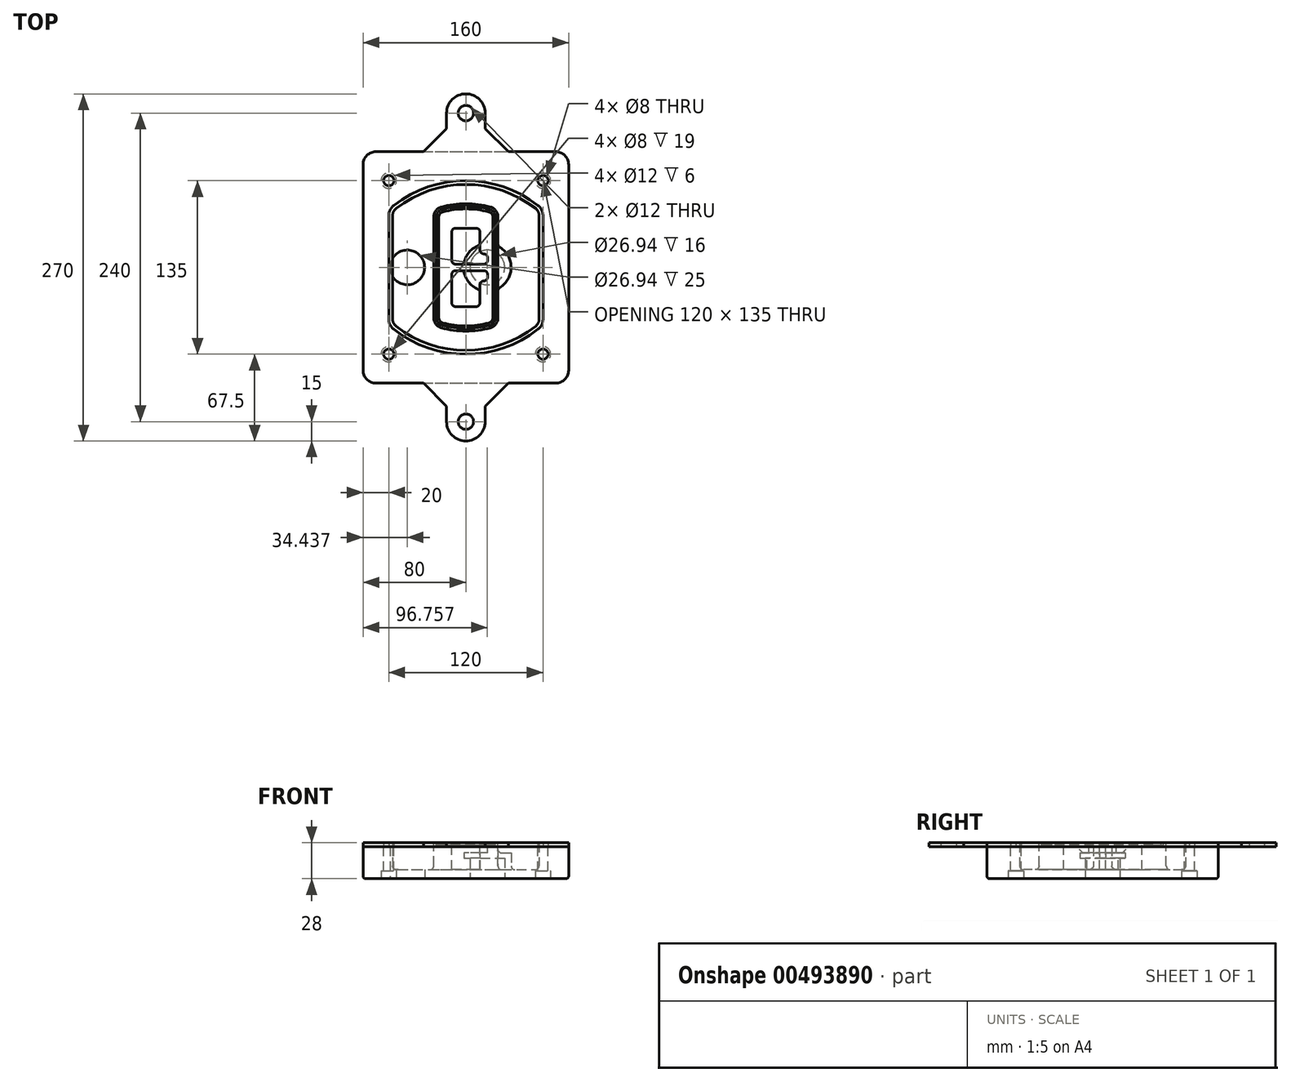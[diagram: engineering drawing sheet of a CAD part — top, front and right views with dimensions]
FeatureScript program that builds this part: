
annotation { "Feature Type Name" : "Feature", "Feature Type Description" : "" }
export const myFeature = defineFeature(function(context is Context, id is Id, definition is map)
    precondition{}
    {
        {
            var Q0;
            Q0=qCreatedBy(makeId("Top.planeOp"),FACE);
            var sketch = newSketch(context, id + "F0", { "sketchPlane" : qUnion([Q0])});
            skPoint(sketch, "E0.rect.middle", {"position": v(0, 0) * mm});
            skLineSegment(sketch, "E1.bottom", {"start": v(-70, -90) * mm, "end": v(70, -90) * mm});
            skLineSegment(sketch, "E1.top", {"start": v(-70, 90) * mm, "end": v(70, 90) * mm});
            skLineSegment(sketch, "E1.left", {"start": v(-80, -80) * mm, "end": v(-80, 80) * mm});
            skLineSegment(sketch, "E1.right", {"start": v(80, -80) * mm, "end": v(80, 80) * mm});
            skLineSegment(sketch, "E2", {"start": v(-80, 90) * mm, "end": v(80, -90) * mm, "construction": true});
            skLineSegment(sketch, "E3", {"start": v(80, 90) * mm, "end": v(-80, -90) * mm, "construction": true});
            skCircle(sketch, "E4", {"center": v(-60, 67.5) * mm, "radius": 4 * mm});
            skCircle(sketch, "E5", {"center": v(60, 67.5) * mm, "radius": 4 * mm});
            skCircle(sketch, "E6", {"center": v(60, -67.5) * mm, "radius": 4 * mm});
            skCircle(sketch, "E7", {"center": v(-60, -67.5) * mm, "radius": 4 * mm});
            skLineSegment(sketch, "E8", {"start": v(-60, 67.5) * mm, "end": v(60, 67.5) * mm, "construction": true});
            skLineSegment(sketch, "E9", {"start": v(60, 67.5) * mm, "end": v(60, -67.5) * mm, "construction": true});
            skLineSegment(sketch, "E10", {"start": v(60, -67.5) * mm, "end": v(-60, -67.5) * mm, "construction": true});
            skLineSegment(sketch, "E11", {"start": v(-60, -67.5) * mm, "end": v(-60, 67.5) * mm, "construction": true});
            skLineSegment(sketch, "E12", {"start": v(-60, 40.3) * mm, "end": v(-60, -40.3) * mm});
            skLineSegment(sketch, "E13", {"start": v(60, 40.3) * mm, "end": v(60, -40.3) * mm});
            skArc(sketch, "E14", {"start": v(56.15, 48.18) * mm, "mid": v(0, 67.5) * mm, "end": v(-56.15, 48.18) * mm});
            skArc(sketch, "E15", {"start": v(-56.15, -48.18) * mm, "mid": v(0, -67.5) * mm, "end": v(56.15, -48.18) * mm});
            skLineSegment(sketch, "E16", {"start": v(-60, 0) * mm, "end": v(60, 0) * mm, "construction": true});
            skPoint(sketch, "E17.visualSharp", {"position": v(-60, -45) * mm});
            skArc(sketch, "E17.filletArc", {"start": v(-60, -40.3) * mm, "mid": v(-58.99, -44.68) * mm, "end": v(-56.15, -48.18) * mm});
            skPoint(sketch, "E18.visualSharp", {"position": v(-60, 45) * mm});
            skArc(sketch, "E18.filletArc", {"start": v(-56.15, 48.18) * mm, "mid": v(-58.99, 44.68) * mm, "end": v(-60, 40.3) * mm});
            skPoint(sketch, "E19.visualSharp", {"position": v(60, 45) * mm});
            skArc(sketch, "E19.filletArc", {"start": v(60, 40.3) * mm, "mid": v(58.99, 44.68) * mm, "end": v(56.15, 48.18) * mm});
            skPoint(sketch, "E20.visualSharp", {"position": v(60, -45) * mm});
            skArc(sketch, "E20.filletArc", {"start": v(56.15, -48.18) * mm, "mid": v(58.99, -44.68) * mm, "end": v(60, -40.3) * mm});
            skPoint(sketch, "E21.visualSharp", {"position": v(-80, 90) * mm});
            skArc(sketch, "E21.filletArc", {"start": v(-70, 90) * mm, "mid": v(-77.07, 87.07) * mm, "end": v(-80, 80) * mm});
            skPoint(sketch, "E22.visualSharp", {"position": v(80, 90) * mm});
            skArc(sketch, "E22.filletArc", {"start": v(80, 80) * mm, "mid": v(77.07, 87.07) * mm, "end": v(70, 90) * mm});
            skPoint(sketch, "E23.visualSharp", {"position": v(80, -90) * mm});
            skArc(sketch, "E23.filletArc", {"start": v(70, -90) * mm, "mid": v(77.07, -87.07) * mm, "end": v(80, -80) * mm});
            skPoint(sketch, "E24.visualSharp", {"position": v(-80, -90) * mm});
            skArc(sketch, "E24.filletArc", {"start": v(-80, -80) * mm, "mid": v(-77.07, -87.07) * mm, "end": v(-70, -90) * mm});
            skArc(sketch, "E25.0", {"start": v(57, 40.3) * mm, "mid": v(56.3, 43.36) * mm, "end": v(54.3, 45.81) * mm});
            skLineSegment(sketch, "E25.1", {"start": v(57, 40.3) * mm, "end": v(57, -40.3) * mm});
            skArc(sketch, "E25.2", {"start": v(54.3, -45.81) * mm, "mid": v(56.3, -43.36) * mm, "end": v(57, -40.3) * mm});
            skArc(sketch, "E25.3", {"start": v(-54.3, -45.81) * mm, "mid": v(0, -64.5) * mm, "end": v(54.3, -45.81) * mm});
            skArc(sketch, "E25.4", {"start": v(-57, -40.3) * mm, "mid": v(-56.3, -43.36) * mm, "end": v(-54.3, -45.81) * mm});
            skArc(sketch, "E25.5", {"start": v(54.3, 45.81) * mm, "mid": v(0, 64.5) * mm, "end": v(-54.3, 45.81) * mm});
            skLineSegment(sketch, "E25.6", {"start": v(-57, 40.3) * mm, "end": v(-57, -40.3) * mm});
            skArc(sketch, "E25.7", {"start": v(-54.3, 45.81) * mm, "mid": v(-56.3, 43.36) * mm, "end": v(-57, 40.3) * mm});
            skArc(sketch, "E26.0", {"start": v(-58.62, 51.33) * mm, "mid": v(-62.58, 46.43) * mm, "end": v(-64, 40.3) * mm});
            skArc(sketch, "E26.1", {"start": v(58.62, 51.33) * mm, "mid": v(0, 71.5) * mm, "end": v(-58.62, 51.33) * mm});
            skArc(sketch, "E26.2", {"start": v(64, 40.3) * mm, "mid": v(62.58, 46.43) * mm, "end": v(58.62, 51.33) * mm});
            skLineSegment(sketch, "E26.3", {"start": v(64, 40.3) * mm, "end": v(64, -40.3) * mm});
            skArc(sketch, "E26.4", {"start": v(58.62, -51.33) * mm, "mid": v(62.58, -46.43) * mm, "end": v(64, -40.3) * mm});
            skLineSegment(sketch, "E26.5", {"start": v(-64, 40.3) * mm, "end": v(-64, -40.3) * mm});
            skArc(sketch, "E26.6", {"start": v(-58.62, -51.33) * mm, "mid": v(0, -71.5) * mm, "end": v(58.62, -51.33) * mm});
            skArc(sketch, "E26.7", {"start": v(-64, -40.3) * mm, "mid": v(-62.58, -46.43) * mm, "end": v(-58.62, -51.33) * mm});
            skSolve(sketch);
        }
        {
            var Q0;
            Q0=makeQuery(id+"F0.imprint","IMPRINT",FACE,{"disambiguationData":[TD([[makeQuery(id+"F0.imprint","IMPRINT",EDGE,{"derivedFrom":sQuery(id+"F0.wireOp",EDGE,"E1.bottom")}),1.0]])]});
            var Q1;
            Q1=makeQuery(id+"F0.imprint","IMPRINT",FACE,{"disambiguationData":[TD([[makeQuery(id+"F0.imprint","IMPRINT",EDGE,{"derivedFrom":sQuery(id+"F0.wireOp",EDGE,"E12")}),1.0]])]});
            var Q2;
            Q2=makeQuery(id+"F0.imprint","IMPRINT",FACE,{"disambiguationData":[TD([[makeQuery(id+"F0.imprint","IMPRINT",EDGE,{"derivedFrom":sQuery(id+"F0.wireOp",EDGE,"E25.0")}),1.0]])]});
            var Q3;
            Q3=makeQuery(id+"F0.imprint","IMPRINT",FACE,{"disambiguationData":[TD([[makeQuery(id+"F0.imprint","IMPRINT",EDGE,{"derivedFrom":sQuery(id+"F0.wireOp",EDGE,"E12")}),-1.0]])]});
            extrude(context, id + "F1", {"entities" : qUnion([Q0, Q1, Q2, Q3]), "oppositeDirection" : true, "depth" : 25 * mm});
        }
        {
            var Q0;
            Q0=makeQuery(id+"F0.imprint","IMPRINT",FACE,{"disambiguationData":[TD([[makeQuery(id+"F0.imprint","IMPRINT",EDGE,{"derivedFrom":sQuery(id+"F0.wireOp",EDGE,"E12")}),1.0]])]});
            extrude(context, id + "F2", {"entities" : qUnion([Q0]), "operationType" : NewBodyOperationType.ADD, "depth" : 3 * mm});
        }
        {
            var Q0;
            Q0=makeQuery(id+"F0.imprint","IMPRINT",FACE,{"disambiguationData":[TD([[makeQuery(id+"F0.imprint","IMPRINT",EDGE,{"derivedFrom":sQuery(id+"F0.wireOp",EDGE,"E25.0")}),1.0]])]});
            extrude(context, id + "F3", {"entities" : qUnion([Q0]), "operationType" : NewBodyOperationType.REMOVE, "oppositeDirection" : true, "depth" : 18 * mm});
        }
        {
            var Q0;
            Q0=makeQuery(id+"F2.opExtrude","CAP_FACE",FACE,{"disambiguationData":[OSD([sQuery(id+"F0.wireOp",EDGE,"E12"),sQuery(id+"F0.wireOp",EDGE,"E13"),sQuery(id+"F0.wireOp",EDGE,"E14"),sQuery(id+"F0.wireOp",EDGE,"E15"),sQuery(id+"F0.wireOp",EDGE,"E17.filletArc"),sQuery(id+"F0.wireOp",EDGE,"E18.filletArc"),sQuery(id+"F0.wireOp",EDGE,"E19.filletArc"),sQuery(id+"F0.wireOp",EDGE,"E20.filletArc"),sQuery(id+"F0.wireOp",EDGE,"E25.0"),sQuery(id+"F0.wireOp",EDGE,"E25.1"),sQuery(id+"F0.wireOp",EDGE,"E25.2"),sQuery(id+"F0.wireOp",EDGE,"E25.3"),sQuery(id+"F0.wireOp",EDGE,"E25.4"),sQuery(id+"F0.wireOp",EDGE,"E25.5"),sQuery(id+"F0.wireOp",EDGE,"E25.6"),sQuery(id+"F0.wireOp",EDGE,"E25.7")])],"isStart":false});
            var sketch = newSketch(context, id + "F4", { "sketchPlane" : qUnion([Q0])});
            skArc(sketch, "E27.0", {"start": v(-19.08, -46.97) * mm, "mid": v(0, -49.5) * mm, "end": v(19.08, -46.97) * mm});
            skArc(sketch, "E28.0", {"start": v(19.08, 46.97) * mm, "mid": v(0, 49.5) * mm, "end": v(-19.08, 46.97) * mm});
            skLineSegment(sketch, "E29", {"start": v(-25, 39.25) * mm, "end": v(-25, -39.25) * mm});
            skLineSegment(sketch, "E30", {"start": v(25, 39.25) * mm, "end": v(25, -39.25) * mm});
            skLineSegment(sketch, "E31", {"start": v(-25, 45.1) * mm, "end": v(25, 45.1) * mm, "construction": true});
            skLineSegment(sketch, "E32", {"start": v(-25, -45.1) * mm, "end": v(25, -45.1) * mm, "construction": true});
            skPoint(sketch, "E33.visualSharp", {"position": v(-25, 45.1) * mm});
            skArc(sketch, "E33.filletArc", {"start": v(-19.08, 46.97) * mm, "mid": v(-23.35, 44.11) * mm, "end": v(-25, 39.25) * mm});
            skPoint(sketch, "E34.visualSharp", {"position": v(25, 45.1) * mm});
            skArc(sketch, "E34.filletArc", {"start": v(25, 39.25) * mm, "mid": v(23.35, 44.11) * mm, "end": v(19.08, 46.97) * mm});
            skPoint(sketch, "E35.visualSharp", {"position": v(25, -45.1) * mm});
            skArc(sketch, "E35.filletArc", {"start": v(19.08, -46.97) * mm, "mid": v(23.35, -44.11) * mm, "end": v(25, -39.25) * mm});
            skPoint(sketch, "E36.visualSharp", {"position": v(-25, -45.1) * mm});
            skArc(sketch, "E36.filletArc", {"start": v(-25, -39.25) * mm, "mid": v(-23.35, -44.11) * mm, "end": v(-19.08, -46.97) * mm});
            skArc(sketch, "E37.0", {"start": v(54.3, 45.81) * mm, "mid": v(0, 64.5) * mm, "end": v(-54.3, 45.81) * mm});
            skArc(sketch, "E37.1", {"start": v(-54.3, 45.81) * mm, "mid": v(-56.3, 43.36) * mm, "end": v(-57, 40.3) * mm});
            skLineSegment(sketch, "E37.2", {"start": v(-57, 40.3) * mm, "end": v(-57, -40.3) * mm});
            skArc(sketch, "E37.3", {"start": v(-57, -40.3) * mm, "mid": v(-56.3, -43.36) * mm, "end": v(-54.3, -45.81) * mm});
            skArc(sketch, "E37.4", {"start": v(-54.3, -45.81) * mm, "mid": v(0, -64.5) * mm, "end": v(54.3, -45.81) * mm});
            skArc(sketch, "E37.5", {"start": v(54.3, -45.81) * mm, "mid": v(56.3, -43.36) * mm, "end": v(57, -40.3) * mm});
            skLineSegment(sketch, "E37.6", {"start": v(57, 40.3) * mm, "end": v(57, -40.3) * mm});
            skArc(sketch, "E37.7", {"start": v(57, 40.3) * mm, "mid": v(56.3, 43.36) * mm, "end": v(54.3, 45.81) * mm});
            skLineSegment(sketch, "E38.0", {"start": v(23, 39.25) * mm, "end": v(23, -39.25) * mm});
            skArc(sketch, "E38.1", {"start": v(18.56, -45.04) * mm, "mid": v(21.76, -42.9) * mm, "end": v(23, -39.25) * mm});
            skArc(sketch, "E38.2", {"start": v(-18.56, -45.04) * mm, "mid": v(0, -47.5) * mm, "end": v(18.56, -45.04) * mm});
            skArc(sketch, "E38.3", {"start": v(-23, -39.25) * mm, "mid": v(-21.76, -42.9) * mm, "end": v(-18.56, -45.04) * mm});
            skLineSegment(sketch, "E38.4", {"start": v(-23, 39.25) * mm, "end": v(-23, -39.25) * mm});
            skArc(sketch, "E38.5", {"start": v(23, 39.25) * mm, "mid": v(21.76, 42.9) * mm, "end": v(18.56, 45.04) * mm});
            skArc(sketch, "E38.6", {"start": v(-18.56, 45.04) * mm, "mid": v(-21.76, 42.9) * mm, "end": v(-23, 39.25) * mm});
            skArc(sketch, "E38.7", {"start": v(18.56, 45.04) * mm, "mid": v(0, 47.5) * mm, "end": v(-18.56, 45.04) * mm});
            skArc(sketch, "E39.0", {"start": v(21, 39.25) * mm, "mid": v(20.18, 41.68) * mm, "end": v(18.04, 43.1) * mm});
            skLineSegment(sketch, "E39.1", {"start": v(21, 39.25) * mm, "end": v(21, -39.25) * mm});
            skArc(sketch, "E39.2", {"start": v(18.04, -43.1) * mm, "mid": v(20.18, -41.68) * mm, "end": v(21, -39.25) * mm});
            skArc(sketch, "E39.3", {"start": v(-18.04, -43.1) * mm, "mid": v(0, -45.5) * mm, "end": v(18.04, -43.1) * mm});
            skArc(sketch, "E39.4", {"start": v(-21, -39.25) * mm, "mid": v(-20.18, -41.68) * mm, "end": v(-18.04, -43.1) * mm});
            skArc(sketch, "E39.5", {"start": v(18.04, 43.1) * mm, "mid": v(0, 45.5) * mm, "end": v(-18.04, 43.1) * mm});
            skLineSegment(sketch, "E39.6", {"start": v(-21, 39.25) * mm, "end": v(-21, -39.25) * mm});
            skArc(sketch, "E39.7", {"start": v(-18.04, 43.1) * mm, "mid": v(-20.18, 41.68) * mm, "end": v(-21, 39.25) * mm});
            skLineSegment(sketch, "E40", {"start": v(-25, 0) * mm, "end": v(25, 0) * mm, "construction": true});
            skLineSegment(sketch, "E41", {"start": v(-11, 5.5) * mm, "end": v(-11, 27.5) * mm});
            skLineSegment(sketch, "E42", {"start": v(-8, 30.5) * mm, "end": v(8, 30.5) * mm});
            skLineSegment(sketch, "E43", {"start": v(11, 27.5) * mm, "end": v(11, 13.5) * mm});
            skLineSegment(sketch, "E44", {"start": v(14, 10.5) * mm, "end": v(14, 10.5) * mm});
            skLineSegment(sketch, "E45", {"start": v(17, 7.5) * mm, "end": v(17, 5.5) * mm});
            skLineSegment(sketch, "E46", {"start": v(14, 2.5) * mm, "end": v(-8, 2.5) * mm});
            skPoint(sketch, "E47.visualSharp", {"position": v(-11, 30.5) * mm});
            skArc(sketch, "E47.filletArc", {"start": v(-8, 30.5) * mm, "mid": v(-10.12, 29.62) * mm, "end": v(-11, 27.5) * mm});
            skPoint(sketch, "E48.visualSharp", {"position": v(11, 30.5) * mm});
            skArc(sketch, "E48.filletArc", {"start": v(11, 27.5) * mm, "mid": v(10.12, 29.62) * mm, "end": v(8, 30.5) * mm});
            skPoint(sketch, "E49.visualSharp", {"position": v(11, 10.5) * mm});
            skArc(sketch, "E49.filletArc", {"start": v(11, 13.5) * mm, "mid": v(11.88, 11.38) * mm, "end": v(14, 10.5) * mm});
            skPoint(sketch, "E50.visualSharp", {"position": v(17, 10.5) * mm});
            skArc(sketch, "E50.filletArc", {"start": v(17, 7.5) * mm, "mid": v(16.12, 9.62) * mm, "end": v(14, 10.5) * mm});
            skPoint(sketch, "E51.visualSharp", {"position": v(17, 2.5) * mm});
            skArc(sketch, "E51.filletArc", {"start": v(14, 2.5) * mm, "mid": v(16.12, 3.38) * mm, "end": v(17, 5.5) * mm});
            skPoint(sketch, "E52.visualSharp", {"position": v(-11, 2.5) * mm});
            skArc(sketch, "E52.filletArc", {"start": v(-11, 5.5) * mm, "mid": v(-10.12, 3.38) * mm, "end": v(-8, 2.5) * mm});
            skLineSegment(sketch, "E53.0.MirrorCS", {"start": v(14, -2.5) * mm, "end": v(-8, -2.5) * mm});
            skArc(sketch, "E54.0.MirrorCS", {"start": v(-11, -5.5) * mm, "mid": v(-10.12, -3.38) * mm, "end": v(-8, -2.5) * mm});
            skLineSegment(sketch, "E55.0.MirrorCS", {"start": v(-11, -5.5) * mm, "end": v(-11, -27.5) * mm});
            skArc(sketch, "E56.0.MirrorCS", {"start": v(-8, -30.5) * mm, "mid": v(-10.12, -29.62) * mm, "end": v(-11, -27.5) * mm});
            skLineSegment(sketch, "E57.0.MirrorCS", {"start": v(-8, -30.5) * mm, "end": v(8, -30.5) * mm});
            skArc(sketch, "E58.0.MirrorCS", {"start": v(11, -27.5) * mm, "mid": v(10.12, -29.62) * mm, "end": v(8, -30.5) * mm});
            skLineSegment(sketch, "E59.0.MirrorCS", {"start": v(11, -27.5) * mm, "end": v(11, -13.5) * mm});
            skArc(sketch, "E60.0.MirrorCS", {"start": v(11, -13.5) * mm, "mid": v(11.88, -11.38) * mm, "end": v(14, -10.5) * mm});
            skArc(sketch, "E61.0.MirrorCS", {"start": v(17, -7.5) * mm, "mid": v(16.12, -9.62) * mm, "end": v(14, -10.5) * mm});
            skLineSegment(sketch, "E62.0.MirrorCS", {"start": v(17, -7.5) * mm, "end": v(17, -5.5) * mm});
            skArc(sketch, "E63.0.MirrorCS", {"start": v(14, -2.5) * mm, "mid": v(16.12, -3.38) * mm, "end": v(17, -5.5) * mm});
            skSolve(sketch);
        }
        {
            var Q0;
            Q0=makeQuery(id+"F4.imprint","IMPRINT",FACE,{"disambiguationData":[TD([[makeQuery(id+"F4.imprint","IMPRINT",EDGE,{"derivedFrom":sQuery(id+"F4.wireOp",EDGE,"E27.0")}),1.0]])]});
            var Q1;
            Q1=makeQuery(id+"F4.imprint","IMPRINT",FACE,{"disambiguationData":[TD([[makeQuery(id+"F4.imprint","IMPRINT",EDGE,{"derivedFrom":sQuery(id+"F4.wireOp",EDGE,"E38.0")}),-1.0]])]});
            var Q2;
            Q2=makeQuery(id+"F4.imprint","IMPRINT",FACE,{"disambiguationData":[TD([[makeQuery(id+"F4.imprint","IMPRINT",EDGE,{"derivedFrom":sQuery(id+"F4.wireOp",EDGE,"E39.0")}),1.0]])]});
            extrude(context, id + "F5", {"entities" : qUnion([Q0, Q1, Q2]), "operationType" : NewBodyOperationType.ADD, "endBound" : BoundingType.UP_TO_NEXT, "oppositeDirection" : true, "depth" : 25 * mm});
        }
        {
            var Q0;
            Q0=makeQuery(id+"F4.imprint","IMPRINT",FACE,{"disambiguationData":[TD([[makeQuery(id+"F4.imprint","IMPRINT",EDGE,{"derivedFrom":sQuery(id+"F4.wireOp",EDGE,"E38.0")}),-1.0]])]});
            extrude(context, id + "F6", {"entities" : qUnion([Q0]), "operationType" : NewBodyOperationType.REMOVE, "oppositeDirection" : true, "depth" : 2 * mm});
        }
        {
            var Q0;
            Q0=makeQuery(id+"F1.opExtrude","CAP_FACE",FACE,{"disambiguationData":[OSD([sQuery(id+"F0.wireOp",EDGE,"E1.bottom"),sQuery(id+"F0.wireOp",EDGE,"E1.top"),sQuery(id+"F0.wireOp",EDGE,"E1.left"),sQuery(id+"F0.wireOp",EDGE,"E1.right"),sQuery(id+"F0.wireOp",EDGE,"E4"),sQuery(id+"F0.wireOp",EDGE,"E5"),sQuery(id+"F0.wireOp",EDGE,"E6"),sQuery(id+"F0.wireOp",EDGE,"E7"),sQuery(id+"F0.wireOp",EDGE,"E21.filletArc"),sQuery(id+"F0.wireOp",EDGE,"E22.filletArc"),sQuery(id+"F0.wireOp",EDGE,"E23.filletArc"),sQuery(id+"F0.wireOp",EDGE,"E24.filletArc")])],"isStart":false});
            var sketch = newSketch(context, id + "F7", { "sketchPlane" : qUnion([Q0])});
            skCircle(sketch, "E64", {"center": v(16.76, 0) * mm, "radius": 13.47 * mm});
            skCircle(sketch, "E65", {"center": v(-45.56, 0) * mm, "radius": 13.47 * mm});
            skLineSegment(sketch, "E66", {"start": v(80, 0) * mm, "end": v(-80, 0) * mm});
            skCircle(sketch, "E67", {"center": v(16.76, 0) * mm, "radius": 18.47 * mm});
            skCircle(sketch, "E68", {"center": v(60, -67.5) * mm, "radius": 6 * mm});
            skCircle(sketch, "E69", {"center": v(-60, -67.5) * mm, "radius": 6 * mm});
            skCircle(sketch, "E70", {"center": v(-60, 67.5) * mm, "radius": 6 * mm});
            skCircle(sketch, "E71", {"center": v(60, 67.5) * mm, "radius": 6 * mm});
            skSolve(sketch);
        }
        {
            var Q0;
            {var subQ1=sQuery(id+"F7.wireOp",EDGE,"E66");var subQ4=sQuery(id+"F7.wireOp",EDGE,"E64");var subQ6=makeQuery(id+"F7.imprint","INTERSECT",VERTEX,{"disambiguationData":[OD(0.0)],"derivedFrom":[subQ4,subQ1]});Q0=makeQuery(id+"F7.imprint","IMPRINT",FACE,{"disambiguationData":[TD([[makeQuery(id+"F7.imprint","IMPRINT",EDGE,{"disambiguationData":[TD([[subQ6,-1.0]])],"derivedFrom":subQ4}),-1.0]])]});}
            var Q1;
            {var subQ0=sQuery(id+"F7.wireOp",EDGE,"E66");var subQ1=sQuery(id+"F7.wireOp",EDGE,"E64");var subQ3=makeQuery(id+"F7.imprint","INTERSECT",VERTEX,{"disambiguationData":[OD(0.0)],"derivedFrom":[subQ1,subQ0]});Q1=makeQuery(id+"F7.imprint","IMPRINT",FACE,{"disambiguationData":[TD([[makeQuery(id+"F7.imprint","IMPRINT",EDGE,{"disambiguationData":[TD([[subQ3,-1.0]])],"derivedFrom":subQ1}),1.0]])]});}
            var Q2;
            {var subQ0=sQuery(id+"F7.wireOp",EDGE,"E66");var subQ1=sQuery(id+"F7.wireOp",EDGE,"E64");var subQ3=makeQuery(id+"F7.imprint","INTERSECT",VERTEX,{"disambiguationData":[OD(0.0)],"derivedFrom":[subQ1,subQ0]});Q2=makeQuery(id+"F7.imprint","IMPRINT",FACE,{"disambiguationData":[TD([[makeQuery(id+"F7.imprint","IMPRINT",EDGE,{"disambiguationData":[TD([[subQ3,1.0]])],"derivedFrom":subQ1}),1.0]])]});}
            var Q3;
            {var subQ1=sQuery(id+"F7.wireOp",EDGE,"E66");var subQ4=sQuery(id+"F7.wireOp",EDGE,"E64");var subQ6=makeQuery(id+"F7.imprint","INTERSECT",VERTEX,{"disambiguationData":[OD(0.0)],"derivedFrom":[subQ4,subQ1]});Q3=makeQuery(id+"F7.imprint","IMPRINT",FACE,{"disambiguationData":[TD([[makeQuery(id+"F7.imprint","IMPRINT",EDGE,{"disambiguationData":[TD([[subQ6,1.0]])],"derivedFrom":subQ4}),-1.0]])]});}
            extrude(context, id + "F8", {"entities" : qUnion([Q0, Q1, Q2, Q3]), "operationType" : NewBodyOperationType.ADD, "oppositeDirection" : true, "depth" : 20 * mm});
        }
        {
            var Q0;
            {var subQ0=sQuery(id+"F7.wireOp",EDGE,"E66");var subQ1=sQuery(id+"F7.wireOp",EDGE,"E64");var subQ3=makeQuery(id+"F7.imprint","INTERSECT",VERTEX,{"disambiguationData":[OD(0.0)],"derivedFrom":[subQ1,subQ0]});Q0=makeQuery(id+"F7.imprint","IMPRINT",FACE,{"disambiguationData":[TD([[makeQuery(id+"F7.imprint","IMPRINT",EDGE,{"disambiguationData":[TD([[subQ3,-1.0]])],"derivedFrom":subQ1}),1.0]])]});}
            var Q1;
            {var subQ0=sQuery(id+"F7.wireOp",EDGE,"E66");var subQ1=sQuery(id+"F7.wireOp",EDGE,"E64");var subQ3=makeQuery(id+"F7.imprint","INTERSECT",VERTEX,{"disambiguationData":[OD(0.0)],"derivedFrom":[subQ1,subQ0]});Q1=makeQuery(id+"F7.imprint","IMPRINT",FACE,{"disambiguationData":[TD([[makeQuery(id+"F7.imprint","IMPRINT",EDGE,{"disambiguationData":[TD([[subQ3,1.0]])],"derivedFrom":subQ1}),1.0]])]});}
            extrude(context, id + "F9", {"entities" : qUnion([Q0, Q1]), "operationType" : NewBodyOperationType.REMOVE, "oppositeDirection" : true, "depth" : 16 * mm});
        }
        {
            var Q0;
            {var subQ0=sQuery(id+"F7.wireOp",EDGE,"E66");var subQ1=sQuery(id+"F7.wireOp",EDGE,"E65");var subQ3=makeQuery(id+"F7.imprint","INTERSECT",VERTEX,{"disambiguationData":[OD(0.0)],"derivedFrom":[subQ1,subQ0]});Q0=makeQuery(id+"F7.imprint","IMPRINT",FACE,{"disambiguationData":[TD([[makeQuery(id+"F7.imprint","IMPRINT",EDGE,{"disambiguationData":[TD([[subQ3,-1.0]])],"derivedFrom":subQ1}),1.0]])]});}
            var Q1;
            {var subQ0=sQuery(id+"F7.wireOp",EDGE,"E66");var subQ1=sQuery(id+"F7.wireOp",EDGE,"E65");var subQ3=makeQuery(id+"F7.imprint","INTERSECT",VERTEX,{"disambiguationData":[OD(0.0)],"derivedFrom":[subQ1,subQ0]});Q1=makeQuery(id+"F7.imprint","IMPRINT",FACE,{"disambiguationData":[TD([[makeQuery(id+"F7.imprint","IMPRINT",EDGE,{"disambiguationData":[TD([[subQ3,1.0]])],"derivedFrom":subQ1}),1.0]])]});}
            extrude(context, id + "F10", {"entities" : qUnion([Q0, Q1]), "operationType" : NewBodyOperationType.REMOVE, "oppositeDirection" : true, "depth" : 25 * mm});
        }
        {
            var Q0;
            Q0=makeQuery(id+"F7.imprint","IMPRINT",FACE,{"disambiguationData":[TD([[makeQuery(id+"F7.imprint","IMPRINT",EDGE,{"derivedFrom":sQuery(id+"F7.wireOp",EDGE,"E68")}),1.0]])]});
            var Q1;
            Q1=makeQuery(id+"F7.imprint","IMPRINT",FACE,{"disambiguationData":[TD([[makeQuery(id+"F7.imprint","IMPRINT",EDGE,{"derivedFrom":makeQuery(id+"F1.opExtrude","CAP_EDGE",EDGE,{"disambiguationData":[OSD([sQuery(id+"F0.wireOp",EDGE,"E5")])],"isStart":false})}),-1.0]])]});
            var Q2;
            Q2=makeQuery(id+"F7.imprint","IMPRINT",FACE,{"disambiguationData":[TD([[makeQuery(id+"F7.imprint","IMPRINT",EDGE,{"derivedFrom":sQuery(id+"F7.wireOp",EDGE,"E69")}),1.0]])]});
            var Q3;
            Q3=makeQuery(id+"F7.imprint","IMPRINT",FACE,{"disambiguationData":[TD([[makeQuery(id+"F7.imprint","IMPRINT",EDGE,{"derivedFrom":makeQuery(id+"F1.opExtrude","CAP_EDGE",EDGE,{"disambiguationData":[OSD([sQuery(id+"F0.wireOp",EDGE,"E4")])],"isStart":false})}),-1.0]])]});
            var Q4;
            Q4=makeQuery(id+"F7.imprint","IMPRINT",FACE,{"disambiguationData":[TD([[makeQuery(id+"F7.imprint","IMPRINT",EDGE,{"derivedFrom":sQuery(id+"F7.wireOp",EDGE,"E70")}),1.0]])]});
            var Q5;
            Q5=makeQuery(id+"F7.imprint","IMPRINT",FACE,{"disambiguationData":[TD([[makeQuery(id+"F7.imprint","IMPRINT",EDGE,{"derivedFrom":makeQuery(id+"F1.opExtrude","CAP_EDGE",EDGE,{"disambiguationData":[OSD([sQuery(id+"F0.wireOp",EDGE,"E7")])],"isStart":false})}),-1.0]])]});
            var Q6;
            Q6=makeQuery(id+"F7.imprint","IMPRINT",FACE,{"disambiguationData":[TD([[makeQuery(id+"F7.imprint","IMPRINT",EDGE,{"derivedFrom":sQuery(id+"F7.wireOp",EDGE,"E71")}),1.0]])]});
            var Q7;
            Q7=makeQuery(id+"F7.imprint","IMPRINT",FACE,{"disambiguationData":[TD([[makeQuery(id+"F7.imprint","IMPRINT",EDGE,{"derivedFrom":makeQuery(id+"F1.opExtrude","CAP_EDGE",EDGE,{"disambiguationData":[OSD([sQuery(id+"F0.wireOp",EDGE,"E6")])],"isStart":false})}),-1.0]])]});
            extrude(context, id + "F11", {"entities" : qUnion([Q0, Q1, Q2, Q3, Q4, Q5, Q6, Q7]), "operationType" : NewBodyOperationType.REMOVE, "oppositeDirection" : true, "depth" : 6 * mm});
        }
        {
            var Q0;
            Q0=makeQuery(id+"F9.boolean.opBoolean","COPY",FACE,{"derivedFrom":makeQuery(id+"F9.opExtrude","CAP_FACE",FACE,{"disambiguationData":[OSD([sQuery(id+"F7.wireOp",EDGE,"E64")])],"isStart":false})});
            var sketch = newSketch(context, id + "F12", { "sketchPlane" : qUnion([Q0])});
            skArc(sketch, "E72.0", {"start": v(11, 17.55) * mm, "mid": v(2.57, 11.82) * mm, "end": v(-1.54, 2.5) * mm});
            skArc(sketch, "E72.1", {"start": v(-1.54, -2.5) * mm, "mid": v(2.57, -11.82) * mm, "end": v(11, -17.55) * mm});
            skLineSegment(sketch, "E73", {"start": v(-1.54, -2.5) * mm, "end": v(14, -2.5) * mm});
            skLineSegment(sketch, "E74.0", {"start": v(14, 2.5) * mm, "end": v(-1.54, 2.5) * mm});
            skArc(sketch, "E74.1", {"start": v(14, 2.5) * mm, "mid": v(16.12, 3.38) * mm, "end": v(17, 5.5) * mm});
            skLineSegment(sketch, "E74.2", {"start": v(17, 7.5) * mm, "end": v(17, 5.5) * mm});
            skArc(sketch, "E74.3", {"start": v(17, 7.5) * mm, "mid": v(16.12, 9.62) * mm, "end": v(14, 10.5) * mm});
            skArc(sketch, "E74.4", {"start": v(11, 13.5) * mm, "mid": v(11.88, 11.38) * mm, "end": v(14, 10.5) * mm});
            skLineSegment(sketch, "E74.5", {"start": v(11, 17.55) * mm, "end": v(11, 13.5) * mm});
            skLineSegment(sketch, "E74.7", {"start": v(14, -2.5) * mm, "end": v(-1.54, -2.5) * mm});
            skArc(sketch, "E74.8", {"start": v(14, -2.5) * mm, "mid": v(16.12, -3.38) * mm, "end": v(17, -5.5) * mm});
            skLineSegment(sketch, "E74.9", {"start": v(17, -7.5) * mm, "end": v(17, -5.5) * mm});
            skArc(sketch, "E74.10", {"start": v(17, -7.5) * mm, "mid": v(16.12, -9.62) * mm, "end": v(14, -10.5) * mm});
            skArc(sketch, "E74.11", {"start": v(11, -13.5) * mm, "mid": v(11.88, -11.38) * mm, "end": v(14, -10.5) * mm});
            skLineSegment(sketch, "E74.12", {"start": v(11, -17.55) * mm, "end": v(11, -13.5) * mm});
            skPoint(sketch, "E75.orphan", {"position": v(11, -27.5) * mm});
            skPoint(sketch, "E76.orphan", {"position": v(-8, -2.5) * mm});
            skPoint(sketch, "E77.orphan", {"position": v(-8, 2.5) * mm});
            skPoint(sketch, "E78.orphan", {"position": v(11, 27.5) * mm});
            skSolve(sketch);
        }
        {
            var Q0;
            {var subQ7=sQuery(id+"F12.wireOp",EDGE,"E72.0");var subQ14=sQuery(id+"F12.wireOp",EDGE,"E72.1");var subQ16=sQuery(id+"F12.wireOp",EDGE,"E74.1");var subQ18=sQuery(id+"F12.wireOp",EDGE,"E74.8");Q0=qUnion([makeQuery(id+"F12.imprint","IMPRINT",FACE,{"disambiguationData":[TD([[makeQuery(id+"F12.imprint","IMPRINT",EDGE,{"derivedFrom":subQ7}),1.0]])]}),makeQuery(id+"F12.imprint","IMPRINT",FACE,{"disambiguationData":[TD([[makeQuery(id+"F12.imprint","IMPRINT",EDGE,{"derivedFrom":subQ14}),1.0]])]}),makeQuery(id+"F12.imprint","IMPRINT",FACE,{"disambiguationData":[TD([[makeQuery(id+"F12.imprint","IMPRINT",EDGE,{"derivedFrom":subQ16}),1.0]])]}),makeQuery(id+"F12.imprint","IMPRINT",FACE,{"disambiguationData":[TD([[makeQuery(id+"F12.imprint","IMPRINT",EDGE,{"derivedFrom":subQ18}),-1.0]])]})]);}
            var Q1;
            Q1=makeQuery(id+"F5.boolean.opBoolean","SPLIT",FACE,{"disambiguationData":[TD([makeQuery(id+"F5.opExtrude","SWEPT_FACE",FACE,{"disambiguationData":[OSD([sQuery(id+"F4.wireOp",EDGE,"E41")])]})])],"derivedFrom":makeQuery(id+"F3.boolean.opBoolean","COPY",FACE,{"derivedFrom":makeQuery(id+"F3.opExtrude","CAP_FACE",FACE,{"disambiguationData":[OSD([sQuery(id+"F0.wireOp",EDGE,"E25.0"),sQuery(id+"F0.wireOp",EDGE,"E25.1"),sQuery(id+"F0.wireOp",EDGE,"E25.2"),sQuery(id+"F0.wireOp",EDGE,"E25.3"),sQuery(id+"F0.wireOp",EDGE,"E25.4"),sQuery(id+"F0.wireOp",EDGE,"E25.5"),sQuery(id+"F0.wireOp",EDGE,"E25.6"),sQuery(id+"F0.wireOp",EDGE,"E25.7")])],"isStart":false})})});
            extrude(context, id + "F13", {"entities" : qUnion([Q0]), "operationType" : NewBodyOperationType.REMOVE, "endBound" : BoundingType.UP_TO_SURFACE, "endBoundEntityFace" : qUnion([Q1]), "depth" : 25 * mm});
        }
        {
            var Q0;
            Q0=makeQuery(id+"F3.boolean.opBoolean","COPY",EDGE,{"derivedFrom":makeQuery(id+"F3.opExtrude","CAP_EDGE",EDGE,{"disambiguationData":[OSD([sQuery(id+"F0.wireOp",EDGE,"E25.6")])],"isStart":false})});
            var Q1;
            Q1=makeQuery(id+"F8.boolean.opBoolean","INTERSECT",EDGE,{"derivedFrom":[makeQuery(id+"F5.opExtrude","SWEPT_FACE",FACE,{"disambiguationData":[OSD([sQuery(id+"F4.wireOp",EDGE,"E30")])]}),makeQuery(id+"F8.opExtrude","CAP_FACE",FACE,{"disambiguationData":[OSD([sQuery(id+"F7.wireOp",EDGE,"E67")])],"isStart":false})]});
            var Q2;
            Q2=makeQuery(id+"F8.boolean.opBoolean","INTERSECT",EDGE,{"disambiguationData":[OD(1.0)],"derivedFrom":[makeQuery(id+"F5.opExtrude","SWEPT_FACE",FACE,{"disambiguationData":[OSD([sQuery(id+"F4.wireOp",EDGE,"E30")])]}),makeQuery(id+"F8.opExtrude","SWEPT_FACE",FACE,{"disambiguationData":[OSD([sQuery(id+"F7.wireOp",EDGE,"E67")])]})]});
            var Q3;
            {var subQ0=sQuery(id+"F4.wireOp",EDGE,"E30");Q3=makeQuery(id+"F8.boolean.opBoolean","SPLIT",EDGE,{"disambiguationData":[TD([makeQuery(id+"F5.opExtrude","SWEPT_FACE",FACE,{"disambiguationData":[OSD([sQuery(id+"F4.wireOp",EDGE,"E35.filletArc")])]})])],"derivedFrom":makeQuery(id+"F5.opExtrude","CAP_EDGE",EDGE,{"disambiguationData":[OSD([subQ0])],"isStart":false})});}
            var Q4;
            {var subQ0=sQuery(id+"F0.wireOp",EDGE,"E25.7");var subQ1=sQuery(id+"F0.wireOp",EDGE,"E25.1");var subQ2=sQuery(id+"F0.wireOp",EDGE,"E25.6");var subQ3=sQuery(id+"F0.wireOp",EDGE,"E25.5");var subQ4=sQuery(id+"F0.wireOp",EDGE,"E25.4");var subQ5=sQuery(id+"F0.wireOp",EDGE,"E25.0");var subQ6=sQuery(id+"F0.wireOp",EDGE,"E25.2");var subQ7=sQuery(id+"F0.wireOp",EDGE,"E25.3");Q4=makeQuery(id+"F8.boolean.opBoolean","INTERSECT",EDGE,{"derivedFrom":[makeQuery(id+"F5.boolean.opBoolean","SPLIT",FACE,{"disambiguationData":[TD([makeQuery(id+"F2.opExtrude","SWEPT_FACE",FACE,{"disambiguationData":[OSD([subQ5])]})])],"derivedFrom":makeQuery(id+"F3.boolean.opBoolean","COPY",FACE,{"derivedFrom":makeQuery(id+"F3.opExtrude","CAP_FACE",FACE,{"disambiguationData":[OSD([subQ5,subQ1,subQ6,subQ7,subQ4,subQ3,subQ2,subQ0])],"isStart":false})})}),makeQuery(id+"F8.opExtrude","SWEPT_FACE",FACE,{"disambiguationData":[OSD([sQuery(id+"F7.wireOp",EDGE,"E67")])]})]});}
            var Q5;
            Q5=makeQuery(id+"F8.boolean.opBoolean","INTERSECT",EDGE,{"disambiguationData":[OD(0.0)],"derivedFrom":[makeQuery(id+"F5.opExtrude","SWEPT_FACE",FACE,{"disambiguationData":[OSD([sQuery(id+"F4.wireOp",EDGE,"E30")])]}),makeQuery(id+"F8.opExtrude","SWEPT_FACE",FACE,{"disambiguationData":[OSD([sQuery(id+"F7.wireOp",EDGE,"E67")])]})]});
            fillet(context, id + "F14", {"entities" : qUnion([Q0, Q1, Q2, Q3, Q4, Q5]), "radius" : 3 * mm, "tangentPropagation" : true, "allowEdgeOverflow" : false});
        }
        {
            var Q0;
            Q0=makeQuery(id+"F1.opExtrude","CAP_EDGE",EDGE,{"disambiguationData":[OSD([sQuery(id+"F0.wireOp",EDGE,"E1.bottom")])],"isStart":false});
            fillet(context, id + "F15", {"entities" : qUnion([Q0]), "radius" : 2 * mm, "tangentPropagation" : true, "allowEdgeOverflow" : false});
        }
        {
            var Q0;
            {var subQ0=sQuery(id+"F0.wireOp",EDGE,"E21.filletArc");var subQ1=sQuery(id+"F0.wireOp",EDGE,"E7");var subQ2=sQuery(id+"F0.wireOp",EDGE,"E6");var subQ3=sQuery(id+"F0.wireOp",EDGE,"E5");var subQ4=sQuery(id+"F0.wireOp",EDGE,"E4");var subQ5=sQuery(id+"F0.wireOp",EDGE,"E22.filletArc");var subQ6=sQuery(id+"F0.wireOp",EDGE,"E1.bottom");var subQ7=sQuery(id+"F0.wireOp",EDGE,"E1.right");var subQ8=sQuery(id+"F0.wireOp",EDGE,"E1.top");var subQ9=sQuery(id+"F0.wireOp",EDGE,"E1.left");var subQ10=sQuery(id+"F0.wireOp",EDGE,"E23.filletArc");var subQ11=sQuery(id+"F0.wireOp",EDGE,"E24.filletArc");Q0=makeQuery(id+"F2.boolean.opBoolean","SPLIT",FACE,{"disambiguationData":[TD([makeQuery(id+"F1.opExtrude","SWEPT_FACE",FACE,{"disambiguationData":[OSD([subQ6])]})])],"derivedFrom":makeQuery(id+"F1.opExtrude","CAP_FACE",FACE,{"disambiguationData":[OSD([subQ6,subQ8,subQ9,subQ7,subQ4,subQ3,subQ2,subQ1,subQ0,subQ5,subQ10,subQ11])],"isStart":true})});}
            var sketch = newSketch(context, id + "F16", { "sketchPlane" : qUnion([Q0])});
            skLineSegment(sketch, "E79", {"start": v(0, 120) * mm, "end": v(0, 90) * mm});
            skPoint(sketch, "E79.startSnap0", {"position": v(0, 90) * mm});
            skLineSegment(sketch, "E80", {"start": v(0, -90) * mm, "end": v(0, -120) * mm});
            skCircle(sketch, "E81", {"center": v(0, 120) * mm, "radius": 6 * mm});
            skCircle(sketch, "E82", {"center": v(0, -120) * mm, "radius": 6 * mm});
            skLineSegment(sketch, "E83", {"start": v(-33, 90) * mm, "end": v(-15, 108) * mm});
            skLineSegment(sketch, "E84", {"start": v(-15, 108) * mm, "end": v(-15, 120) * mm});
            skLineSegment(sketch, "E85", {"start": v(33, 90) * mm, "end": v(15, 108) * mm});
            skLineSegment(sketch, "E86", {"start": v(15, 108) * mm, "end": v(15, 120) * mm});
            skArc(sketch, "E87", {"start": v(15, 120) * mm, "mid": v(0, 135) * mm, "end": v(-15, 120) * mm});
            skLineSegment(sketch, "E88", {"start": v(-33, -90) * mm, "end": v(-15, -108) * mm});
            skLineSegment(sketch, "E89", {"start": v(-15, -108) * mm, "end": v(-15, -120) * mm});
            skLineSegment(sketch, "E90", {"start": v(33, -90) * mm, "end": v(15, -108) * mm});
            skLineSegment(sketch, "E91", {"start": v(15, -108) * mm, "end": v(15, -120) * mm});
            skArc(sketch, "E92", {"start": v(-15, -120) * mm, "mid": v(0, -135) * mm, "end": v(15, -120) * mm});
            skSolve(sketch);
        }
        {
            var Q0;
            Q0=makeQuery(id+"F16.imprint","IMPRINT",FACE,{"disambiguationData":[TD([[makeQuery(id+"F16.imprint","IMPRINT",EDGE,{"derivedFrom":makeQuery(id+"F1.opExtrude","CAP_EDGE",EDGE,{"disambiguationData":[OSD([sQuery(id+"F0.wireOp",EDGE,"E1.left")])],"isStart":true})}),-1.0]])]});
            var Q1;
            Q1=makeQuery(id+"F16.imprint","IMPRINT",FACE,{"disambiguationData":[TD([[makeQuery(id+"F16.imprint","IMPRINT",EDGE,{"derivedFrom":sQuery(id+"F16.wireOp",EDGE,"E81")}),-1.0]])]});
            var Q2;
            Q2=makeQuery(id+"F16.imprint","IMPRINT",FACE,{"disambiguationData":[TD([[makeQuery(id+"F16.imprint","IMPRINT",EDGE,{"derivedFrom":sQuery(id+"F16.wireOp",EDGE,"E82")}),-1.0]])]});
            var Q3;
            Q3=makeQuery(id+"F2.opExtrude","CAP_FACE",FACE,{"disambiguationData":[OSD([sQuery(id+"F0.wireOp",EDGE,"E12"),sQuery(id+"F0.wireOp",EDGE,"E13"),sQuery(id+"F0.wireOp",EDGE,"E14"),sQuery(id+"F0.wireOp",EDGE,"E15"),sQuery(id+"F0.wireOp",EDGE,"E17.filletArc"),sQuery(id+"F0.wireOp",EDGE,"E18.filletArc"),sQuery(id+"F0.wireOp",EDGE,"E19.filletArc"),sQuery(id+"F0.wireOp",EDGE,"E20.filletArc"),sQuery(id+"F0.wireOp",EDGE,"E25.0"),sQuery(id+"F0.wireOp",EDGE,"E25.1"),sQuery(id+"F0.wireOp",EDGE,"E25.2"),sQuery(id+"F0.wireOp",EDGE,"E25.3"),sQuery(id+"F0.wireOp",EDGE,"E25.4"),sQuery(id+"F0.wireOp",EDGE,"E25.5"),sQuery(id+"F0.wireOp",EDGE,"E25.6"),sQuery(id+"F0.wireOp",EDGE,"E25.7")])],"isStart":false});
            extrude(context, id + "F17", {"entities" : qUnion([Q0, Q1, Q2]), "endBound" : BoundingType.UP_TO_SURFACE, "endBoundEntityFace" : qUnion([Q3]), "depth" : 25 * mm});
        }
    });
